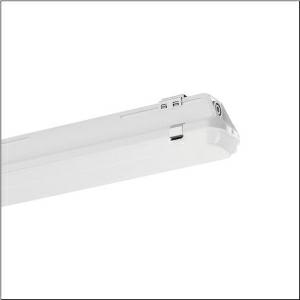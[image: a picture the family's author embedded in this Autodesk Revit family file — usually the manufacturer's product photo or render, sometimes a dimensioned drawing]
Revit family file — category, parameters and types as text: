
# Revit family: monsun_11_facade_51ff40mp460h
name_source: partatom
category: Lighting Fixtures
units: mm (PartAtom-declared; Revit-internal decimal feet)

## family parameters
Cut with Voids When Loaded = No
Host = Face
Light Source = No
Part Type = Normal
Room Calculation Point = No
Round Connector Dimension = Use Diameter
Shared = No

## types (1)
- --- (1 x LED, 6110 lm, 33.5 W, 4000K)
    Apparent Load = 34 VA
    CIE Flux Codes = 47 77 93 95 100
    Color Rendering = 80
    Color Temperature = 4000K
    Default Elevation = 1800 mm
    Description = Monsun 11 facade, damp-proof luminaire, chain hanger, primary optical cover: enclosure, of PMMA, light emission: direct distribution, primary light characteristic: symmetric, installation type: surface-mounted, horizontal mounting, vertical mounting, LED, rated luminous flux: 6.110lm, luminous efficacy: 182lm/W, light colour: 840, colour temperature: 4000K, control gear: ON/OFF Multilumen, with terminal, 3-pole, max. 2.5mm², mains connection: 220..240V, AC, 50/60Hz, rated input power: 34W, luminaire housing, of glass-fibre reinforced polyester, uncoated, bright grey, incl. chain hanger, for cables, Ø 8.4..12mm, with climate membrane, length: 1.590mm, width: 90mm, height: 88mm, clip for enclosure, of stainless steel (V2A), ceiling mounting element, of stainless steel (V2A), chain hanger, of stainless steel (V2A), protection rating (complete): IP66, insulation class (complete): insulation class I (protective earthing), certification: CE, ENEC, VDE, UKCA, protection symbol: D, impact resistance: IK06, permissible operating ambient temperature: -35..+50°C, standard: EN 50419, EN 60598-2-1, contact your sales advisor before using the luminaires in applications with unclear chemical exposure, large temperature fluctuations or condensation-forming humidity, LABS conformity tested according to VDMA 24364:2018-05, exposed outdoor area, packaging unit: 1 piece
    Height = 89 mm
    Lamp = 1 x LED
    Lamp Light Flux = 6110 lm
    Lamp Power = 33.5 W
    Lamp count = 1
    Length = 1590 mm
    Luminous efficacy = 182 lm/W
    Manufacturer = Siteco
    ModVariant = No
    Model = 51FF40MP460H
    Mounting Place = Ceiling
    Mounting Type = Surface mounted
    Number of Poles = 1
    OnlyDefault = Yes
    Power Factor = 1
    Product Name = Monsun 11 facade
    Product group = damp-proof luminaire
    ProductGroupID = 300
    Protection Class = Protection class I
    Protection Degree = IP 66
    RLX_Detail_Level = 1
    RLX_Emergency_Light_Flux = 0 lm
    RLX_Emergency_Type = 0
    RLX_Emergency_Type_DB = No
    RlxData = <blob elided: 89541 chars, md5=c1b9c858>
    Socket = socket
    Standby Power = 0 W
    System Light Flux = 6110 lm
    System Power = 34 W
    Type Comments = factory setting: luminous flux: 100 % | (A | C | E) | 77 mA
    Type Image = l_1349237.jpg
    URL = http://relux.com
    VarID = @adj_195911
    Voltage = 0 V
    Weight = 0.00 kg
    Width = 90 mm

## geometry (parser evidence)
native form markers: Blend x4, Sweep x15
no freeform markers — native parametric forms only
